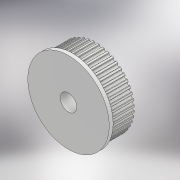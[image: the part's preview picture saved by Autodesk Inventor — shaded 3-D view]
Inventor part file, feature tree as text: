
AUTODESK INVENTOR PART (.ipt)
format: ipt  version: 2018.2 (Build 222227000, 227)  size: 374,272 bytes
history: native  units: mm
features: extrude x6, sketch x5, pattern_circular x1
ambient origin geometry x8: Origin, YZ Plane, XZ Plane, XY Plane, X Axis, Y Axis, Z Axis, Center Point
bodies: Solid1 (feature_tree)
feature tree (12):
  extrude  "Extrusion1"  Depth=0.5mm
  extrude  "Extrusion2"  Depth=7.0mm TaperAngle=0.0deg
  pattern_circular  "Circular Pattern1"  [2 undecoded]
  extrude  "Extrusion3"  Depth=1.0mm TaperAngle=0.0deg
  sketch  "Sketch4"  dims[d18=6.35mm]
  extrude  "Extrusion4"  Depth=6.0mm TaperAngle=0.0deg
  extrude  "Extrusion5"  Depth=3.0mm
  extrude  "Extrusion6"  Depth=6.0mm TaperAngle=0.0deg
  sketch  "Sketch1"  dims[d8=0.0mm d9=0.5mm]
  sketch  "Sketch2"  dims[d10=0.15mm d12=7.0mm d13=0.0mm]
  sketch  "Sketch3"  dims[d15=360.0deg]
  sketch  "Sketch5"  dims[d20=0.0mm d21=2.0mm d22=1.0mm d23=0.0mm d24=6.0mm d25=0.0mm d26=3.0mm d27=6.0mm d28=0.0mm]
note: 2 required parameter values undecoded (feature->parameter linkage not recoverable at this tier; creation-order binding heuristic only, values carry confidence <= 0.55)
